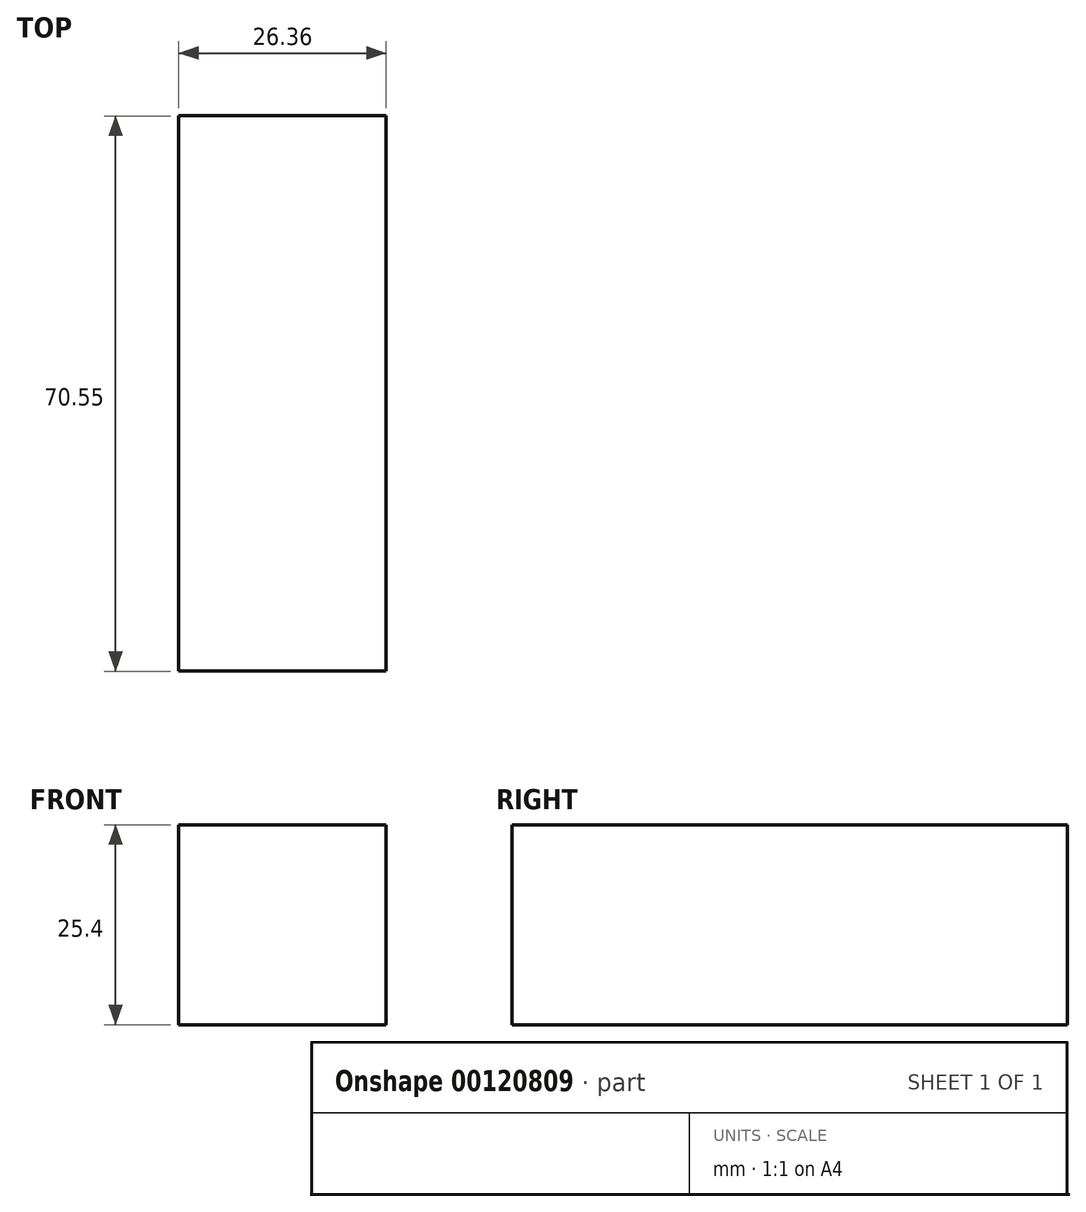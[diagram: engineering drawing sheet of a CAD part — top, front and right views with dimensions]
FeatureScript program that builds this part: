
annotation { "Feature Type Name" : "Feature", "Feature Type Description" : "" }
export const myFeature = defineFeature(function(context is Context, id is Id, definition is map)
    precondition{}
    {
        {
            var Q0;
            Q0=qCreatedBy(makeId("Front.planeOp"),FACE);
            var sketch = newSketch(context, id + "F0", { "sketchPlane" : qUnion([Q0])});
            skCircle(sketch, "E0", {"center": v(0, 0) * mm, "radius": 31.75 * mm});
            skSolve(sketch);
        }
        {
            var Q0;
            Q0=sQuery(id+"F0.wireOp",EDGE,"E0");
            extrude(context, id + "F1", {"bodyType" : ToolBodyType.SURFACE, "surfaceEntities" : qUnion([Q0]), "depth" : 127 * mm});
        }
        {
            var Q0;
            Q0=qCreatedBy(makeId("Top.planeOp"),FACE);
            var sketch = newSketch(context, id + "F2", { "sketchPlane" : qUnion([Q0])});
            skLineSegment(sketch, "E1.bottom", {"start": v(38.6, -35.72) * mm, "end": v(64.95, -35.72) * mm});
            skLineSegment(sketch, "E1.top", {"start": v(38.6, 34.83) * mm, "end": v(64.95, 34.83) * mm});
            skLineSegment(sketch, "E1.left", {"start": v(38.6, -35.72) * mm, "end": v(38.6, 34.83) * mm});
            skLineSegment(sketch, "E1.right", {"start": v(64.95, -35.72) * mm, "end": v(64.95, 34.83) * mm});
            skSolve(sketch);
        }
        {
            var Q0;
            Q0=makeQuery(id+"F2.imprint","IMPRINT",FACE,{"disambiguationData":[TD([[makeQuery(id+"F2.imprint","IMPRINT",EDGE,{"derivedFrom":sQuery(id+"F2.wireOp",EDGE,"E1.bottom")}),1.0]])]});
            extrude(context, id + "F3", {"entities" : qUnion([Q0]), "depth" : 25.4 * mm});
        }
    });
